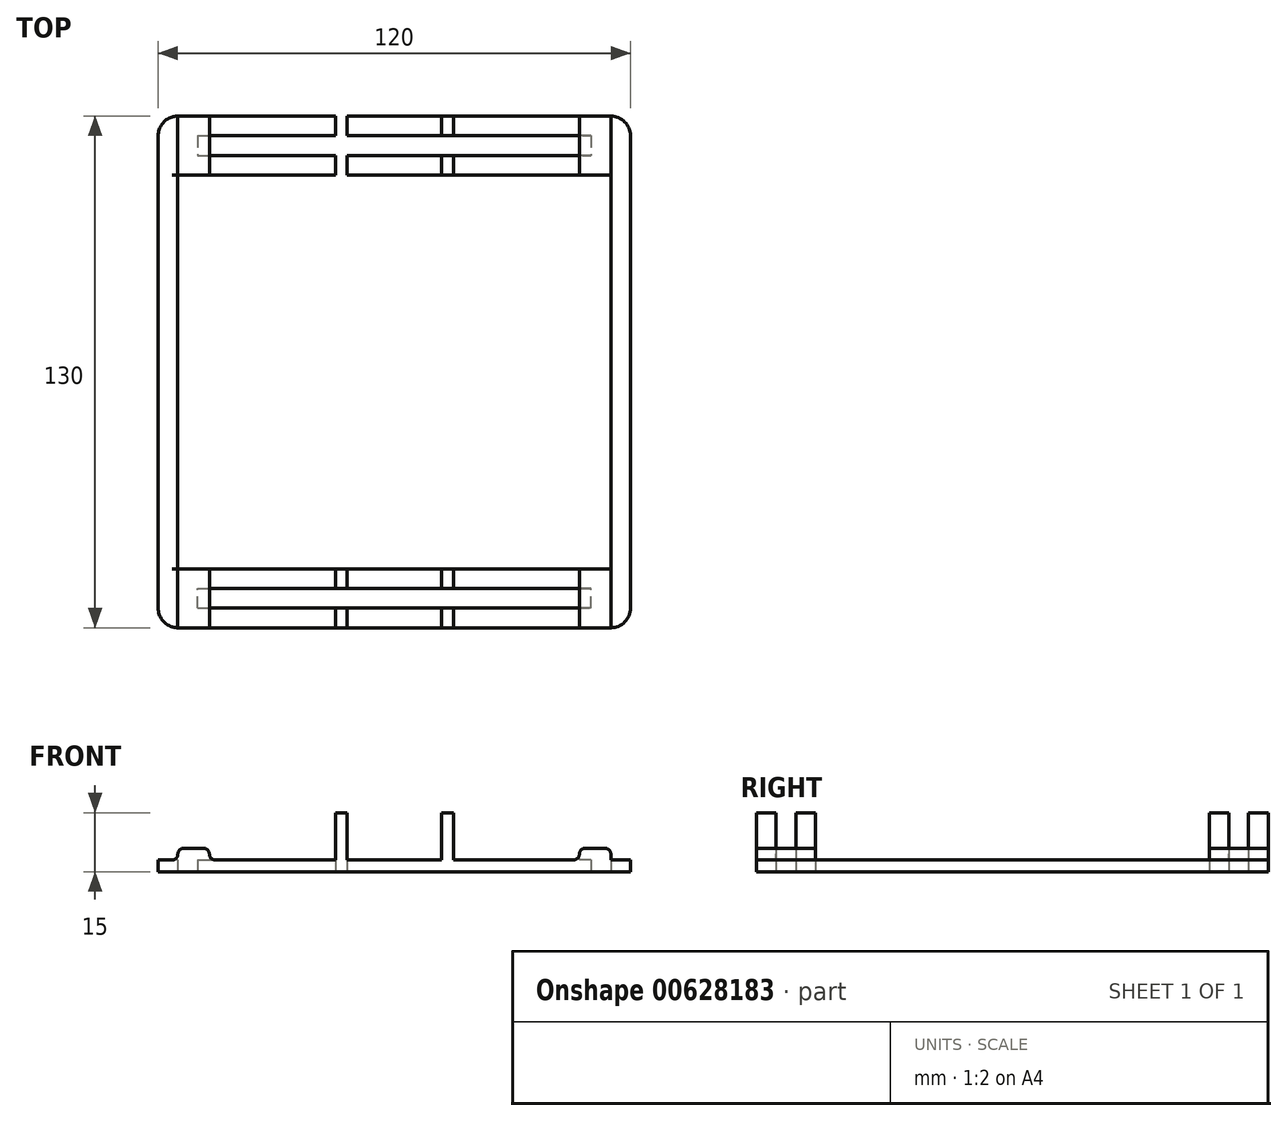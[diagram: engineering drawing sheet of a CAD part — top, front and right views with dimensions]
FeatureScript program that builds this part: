
annotation { "Feature Type Name" : "Feature", "Feature Type Description" : "" }
export const myFeature = defineFeature(function(context is Context, id is Id, definition is map)
    precondition{}
    {
        {
            var Q0;
            Q0=qCreatedBy(makeId("Top.planeOp"),FACE);
            var sketch = newSketch(context, id + "F0", { "sketchPlane" : qUnion([Q0])});
            skLineSegment(sketch, "E0.bottom", {"start": v(-50, 55) * mm, "end": v(50, 55) * mm});
            skLineSegment(sketch, "E0.left", {"start": v(-55, 50) * mm, "end": v(-55, -50) * mm});
            skLineSegment(sketch, "E0.right", {"start": v(55, 50) * mm, "end": v(55, -50) * mm});
            skPoint(sketch, "E0.middle", {"position": v(0, 0) * mm});
            skLineSegment(sketch, "E1.left", {"start": v(-60, 55) * mm, "end": v(-60, -55) * mm});
            skLineSegment(sketch, "E1.right", {"start": v(60, 55) * mm, "end": v(60, -55) * mm});
            skPoint(sketch, "E2.visualSharp", {"position": v(-55, 55) * mm});
            skPoint(sketch, "E3.visualSharp", {"position": v(-60, 60) * mm});
            skPoint(sketch, "E4.visualSharp", {"position": v(55, 55) * mm});
            skPoint(sketch, "E5.visualSharp", {"position": v(60, 60) * mm});
            skPoint(sketch, "E6.visualSharp", {"position": v(55, -55) * mm});
            skPoint(sketch, "E7.visualSharp", {"position": v(60, -60) * mm});
            skPoint(sketch, "E8.visualSharp", {"position": v(-55, -55) * mm});
            skPoint(sketch, "E9.visualSharp", {"position": v(-60, -60) * mm});
            skLineSegment(sketch, "E10", {"start": v(-55, 50) * mm, "end": v(55, 50) * mm});
            skLineSegment(sketch, "E11", {"start": v(-50, 60) * mm, "end": v(-50, 55) * mm});
            skLineSegment(sketch, "E12", {"start": v(50, 60) * mm, "end": v(50, 55) * mm});
            skPoint(sketch, "E13.bottom.end.orphan", {"position": v(15, 55) * mm});
            skPoint(sketch, "E13.bottom.start.orphan", {"position": v(-15, 55) * mm});
            skPoint(sketch, "E13.top.end.orphan", {"position": v(0, 60) * mm});
            skPoint(sketch, "E14.orphan", {"position": v(-15, 60) * mm});
            skPoint(sketch, "E15.orphan", {"position": v(15, 60) * mm});
            skPoint(sketch, "E16.MirrorCS.end.orphan", {"position": v(-15, -60) * mm});
            skPoint(sketch, "E16.MirrorCS.start.orphan", {"position": v(-15, -55) * mm});
            skPoint(sketch, "E17.MirrorCS.end.orphan", {"position": v(15, -60) * mm});
            skPoint(sketch, "E0.top.start.orphan", {"position": v(15, -55) * mm});
            skPoint(sketch, "E1.bottom.start.orphan", {"position": v(-55, 60) * mm});
            skPoint(sketch, "E18.trimOffspring.end.orphan", {"position": v(55, 60) * mm});
            skLineSegment(sketch, "E19", {"start": v(-50, 60) * mm, "end": v(50, 60) * mm});
            skPoint(sketch, "E20", {"position": v(-55, 65) * mm});
            skLineSegment(sketch, "E21", {"start": v(-55, 65) * mm, "end": v(55, 65) * mm});
            skLineSegment(sketch, "E22", {"start": v(-60, 55) * mm, "end": v(-60, 60) * mm});
            skLineSegment(sketch, "E23", {"start": v(-60, 60) * mm, "end": v(-60, 65) * mm});
            skLineSegment(sketch, "E24", {"start": v(-60, 65) * mm, "end": v(-55, 65) * mm});
            skLineSegment(sketch, "E25", {"start": v(60, 55) * mm, "end": v(60, 60) * mm});
            skLineSegment(sketch, "E26", {"start": v(60, 60) * mm, "end": v(60, 65) * mm});
            skLineSegment(sketch, "E27", {"start": v(60, 65) * mm, "end": v(55, 65) * mm});
            skLineSegment(sketch, "E28.MirrorCS", {"start": v(-55, -50) * mm, "end": v(55, -50) * mm});
            skLineSegment(sketch, "E29.MirrorCS", {"start": v(-50, -55) * mm, "end": v(50, -55) * mm});
            skLineSegment(sketch, "E30.MirrorCS", {"start": v(-50, -60) * mm, "end": v(50, -60) * mm});
            skLineSegment(sketch, "E31.MirrorCS", {"start": v(-50, -60) * mm, "end": v(-50, -55) * mm});
            skLineSegment(sketch, "E32.MirrorCS", {"start": v(50, -60) * mm, "end": v(50, -55) * mm});
            skLineSegment(sketch, "E33.MirrorCS", {"start": v(60, -55) * mm, "end": v(60, -60) * mm});
            skLineSegment(sketch, "E34.MirrorCS", {"start": v(60, -60) * mm, "end": v(60, -65) * mm});
            skLineSegment(sketch, "E35.MirrorCS", {"start": v(60, -65) * mm, "end": v(55, -65) * mm});
            skLineSegment(sketch, "E36.MirrorCS", {"start": v(-55, -65) * mm, "end": v(55, -65) * mm});
            skLineSegment(sketch, "E37.MirrorCS", {"start": v(-60, -65) * mm, "end": v(-55, -65) * mm});
            skLineSegment(sketch, "E38.MirrorCS", {"start": v(-60, -60) * mm, "end": v(-60, -65) * mm});
            skLineSegment(sketch, "E39.MirrorCS", {"start": v(-60, -55) * mm, "end": v(-60, -60) * mm});
            skLineSegment(sketch, "E40.bottom", {"start": v(-15, 55) * mm, "end": v(-12, 55) * mm});
            skLineSegment(sketch, "E40.top", {"start": v(-15, 50) * mm, "end": v(-12, 50) * mm});
            skLineSegment(sketch, "E40.left", {"start": v(-15, 55) * mm, "end": v(-15, 50) * mm});
            skLineSegment(sketch, "E40.right", {"start": v(-12, 55) * mm, "end": v(-12, 50) * mm});
            skLineSegment(sketch, "E41.MirrorCS", {"start": v(12, 55) * mm, "end": v(12, 50) * mm});
            skLineSegment(sketch, "E42.MirrorCS", {"start": v(15, 55) * mm, "end": v(15, 50) * mm});
            skLineSegment(sketch, "E43.bottom", {"start": v(-15, 60) * mm, "end": v(-12, 60) * mm});
            skLineSegment(sketch, "E43.top", {"start": v(-15, 65) * mm, "end": v(-12, 65) * mm});
            skLineSegment(sketch, "E43.left", {"start": v(-15, 60) * mm, "end": v(-15, 65) * mm});
            skLineSegment(sketch, "E43.right", {"start": v(-12, 60) * mm, "end": v(-12, 65) * mm});
            skLineSegment(sketch, "E44.MirrorCS", {"start": v(12, 60) * mm, "end": v(12, 65) * mm});
            skLineSegment(sketch, "E45.MirrorCS", {"start": v(15, 60) * mm, "end": v(15, 65) * mm});
            skLineSegment(sketch, "E46.MirrorCS", {"start": v(-15, -55) * mm, "end": v(-15, -50) * mm});
            skLineSegment(sketch, "E47.MirrorCS", {"start": v(-12, -55) * mm, "end": v(-12, -50) * mm});
            skLineSegment(sketch, "E48.MirrorCS", {"start": v(-12, -60) * mm, "end": v(-12, -65) * mm});
            skLineSegment(sketch, "E49.MirrorCS", {"start": v(-15, -60) * mm, "end": v(-15, -65) * mm});
            skLineSegment(sketch, "E50.MirrorCS", {"start": v(12, -60) * mm, "end": v(12, -65) * mm});
            skLineSegment(sketch, "E51.MirrorCS", {"start": v(15, -60) * mm, "end": v(15, -65) * mm});
            skLineSegment(sketch, "E52.MirrorCS", {"start": v(15, -55) * mm, "end": v(15, -50) * mm});
            skLineSegment(sketch, "E53.MirrorCS", {"start": v(12, -55) * mm, "end": v(12, -50) * mm});
            skSolve(sketch);
        }
        {
            var Q0;
            Q0=makeQuery(id+"F0.imprint","IMPRINT",FACE,{"disambiguationData":[TD([[makeQuery(id+"F0.imprint","IMPRINT",EDGE,{"derivedFrom":sQuery(id+"F0.wireOp",EDGE,"E0.left")}),-1.0]])]});
            var Q1;
            Q1=makeQuery(id+"F0.imprint","IMPRINT",FACE,{"disambiguationData":[TD([[makeQuery(id+"F0.imprint","IMPRINT",EDGE,{"derivedFrom":sQuery(id+"F0.wireOp",EDGE,"E0.right")}),1.0]])]});
            extrude(context, id + "F1", {"entities" : qUnion([Q0, Q1]), "depth" : 3 * mm, "offsetDistance" : 25 * mm});
        }
        {
            var Q0;
            Q0=makeQuery(id+"F0.imprint","IMPRINT",FACE,{"disambiguationData":[TD([[makeQuery(id+"F0.imprint","IMPRINT",EDGE,{"derivedFrom":sQuery(id+"F0.wireOp",EDGE,"E43.bottom")}),1.0]])]});
            var Q1;
            Q1=makeQuery(id+"F0.imprint","IMPRINT",FACE,{"disambiguationData":[TD([[makeQuery(id+"F0.imprint","IMPRINT",EDGE,{"derivedFrom":sQuery(id+"F0.wireOp",EDGE,"E40.bottom")}),-1.0]])]});
            var Q2;
            {var subQ0=sQuery(id+"F0.wireOp",EDGE,"E41.MirrorCS");Q2=makeQuery(id+"F0.imprint","IMPRINT",FACE,{"disambiguationData":[TD([[makeQuery(id+"F0.imprint","IMPRINT",EDGE,{"derivedFrom":subQ0}),1.0]])]});}
            var Q3;
            {var subQ0=sQuery(id+"F0.wireOp",EDGE,"E44.MirrorCS");Q3=makeQuery(id+"F0.imprint","IMPRINT",FACE,{"disambiguationData":[TD([[makeQuery(id+"F0.imprint","IMPRINT",EDGE,{"derivedFrom":subQ0}),-1.0]])]});}
            var Q4;
            {var subQ0=sQuery(id+"F0.wireOp",EDGE,"E52.MirrorCS");Q4=makeQuery(id+"F0.imprint","IMPRINT",FACE,{"disambiguationData":[TD([[makeQuery(id+"F0.imprint","IMPRINT",EDGE,{"derivedFrom":subQ0}),1.0]])]});}
            var Q5;
            {var subQ0=sQuery(id+"F0.wireOp",EDGE,"E50.MirrorCS");Q5=makeQuery(id+"F0.imprint","IMPRINT",FACE,{"disambiguationData":[TD([[makeQuery(id+"F0.imprint","IMPRINT",EDGE,{"derivedFrom":subQ0}),1.0]])]});}
            var Q6;
            {var subQ0=sQuery(id+"F0.wireOp",EDGE,"E48.MirrorCS");Q6=makeQuery(id+"F0.imprint","IMPRINT",FACE,{"disambiguationData":[TD([[makeQuery(id+"F0.imprint","IMPRINT",EDGE,{"derivedFrom":subQ0}),-1.0]])]});}
            var Q7;
            {var subQ0=sQuery(id+"F0.wireOp",EDGE,"E46.MirrorCS");Q7=makeQuery(id+"F0.imprint","IMPRINT",FACE,{"disambiguationData":[TD([[makeQuery(id+"F0.imprint","IMPRINT",EDGE,{"derivedFrom":subQ0}),-1.0]])]});}
            extrude(context, id + "F2", {"entities" : qUnion([Q0, Q1, Q2, Q3, Q4, Q5, Q6, Q7]), "depth" : 15 * mm, "offsetDistance" : 25 * mm});
        }
        {
            var Q0;
            {var subQ0=sQuery(id+"F0.wireOp",EDGE,"E43.right");Q0=makeQuery(id+"F0.imprint","IMPRINT",FACE,{"disambiguationData":[TD([[makeQuery(id+"F0.imprint","IMPRINT",EDGE,{"derivedFrom":subQ0}),-1.0]])]});}
            var Q1;
            {var subQ0=sQuery(id+"F0.wireOp",EDGE,"E40.right");Q1=makeQuery(id+"F0.imprint","IMPRINT",FACE,{"disambiguationData":[TD([[makeQuery(id+"F0.imprint","IMPRINT",EDGE,{"derivedFrom":subQ0}),1.0]])]});}
            var Q2;
            {var subQ0=sQuery(id+"F0.wireOp",EDGE,"E47.MirrorCS");Q2=makeQuery(id+"F0.imprint","IMPRINT",FACE,{"disambiguationData":[TD([[makeQuery(id+"F0.imprint","IMPRINT",EDGE,{"derivedFrom":subQ0}),-1.0]])]});}
            var Q3;
            {var subQ0=sQuery(id+"F0.wireOp",EDGE,"E48.MirrorCS");Q3=makeQuery(id+"F0.imprint","IMPRINT",FACE,{"disambiguationData":[TD([[makeQuery(id+"F0.imprint","IMPRINT",EDGE,{"derivedFrom":subQ0}),1.0]])]});}
            extrude(context, id + "F3", {"entities" : qUnion([Q0, Q1, Q2, Q3]), "depth" : 3 * mm, "offsetDistance" : 25 * mm});
        }
        {
            var Q0;
            Q0=makeQuery(id+"F1.opExtrude","SWEPT_EDGE",EDGE,{"disambiguationData":[OSD([sQuery(id+"F0.wireOp",EDGE,"E34.MirrorCS"),sQuery(id+"F0.wireOp",EDGE,"E35.MirrorCS")])]});
            var Q1;
            Q1=makeQuery(id+"F1.opExtrude","SWEPT_EDGE",EDGE,{"disambiguationData":[OSD([sQuery(id+"F0.wireOp",EDGE,"E26"),sQuery(id+"F0.wireOp",EDGE,"E27")])]});
            var Q2;
            Q2=makeQuery(id+"F1.opExtrude","SWEPT_EDGE",EDGE,{"disambiguationData":[OSD([sQuery(id+"F0.wireOp",EDGE,"E37.MirrorCS"),sQuery(id+"F0.wireOp",EDGE,"E38.MirrorCS")])]});
            var Q3;
            Q3=makeQuery(id+"F1.opExtrude","SWEPT_EDGE",EDGE,{"disambiguationData":[OSD([sQuery(id+"F0.wireOp",EDGE,"E23"),sQuery(id+"F0.wireOp",EDGE,"E24")])]});
            fillet(context, id + "F4", {"entities" : qUnion([Q0, Q1, Q2, Q3]), "radius" : 5 * mm, "tangentPropagation" : true, "allowEdgeOverflow" : false});
        }
        {
            var Q0;
            Q0=qCreatedBy(makeId("Front.planeOp"),FACE);
            var sketch = newSketch(context, id + "F5", { "sketchPlane" : qUnion([Q0])});
            skLineSegment(sketch, "E54.bottom", {"start": v(-55, 3) * mm, "end": v(-47, 3) * mm});
            skLineSegment(sketch, "E54.top", {"start": v(-55, 6) * mm, "end": v(-47, 6) * mm});
            skLineSegment(sketch, "E54.left", {"start": v(-55, 3) * mm, "end": v(-55, 6) * mm});
            skLineSegment(sketch, "E54.right", {"start": v(-47, 3) * mm, "end": v(-47, 6) * mm});
            skLineSegment(sketch, "E55.MirrorCS", {"start": v(55, 3) * mm, "end": v(47, 3) * mm});
            skLineSegment(sketch, "E56.MirrorCS", {"start": v(47, 3) * mm, "end": v(47, 6) * mm});
            skLineSegment(sketch, "E57.MirrorCS", {"start": v(55, 6) * mm, "end": v(47, 6) * mm});
            skLineSegment(sketch, "E58.MirrorCS", {"start": v(55, 3) * mm, "end": v(55, 6) * mm});
            skSolve(sketch);
        }
        {
            var Q0;
            Q0=makeQuery(id+"F5.imprint","IMPRINT",FACE,{"disambiguationData":[TD([[makeQuery(id+"F5.imprint","IMPRINT",EDGE,{"derivedFrom":sQuery(id+"F5.wireOp",EDGE,"E54.bottom")}),1.0]])]});
            var Q1;
            Q1=makeQuery(id+"F5.imprint","IMPRINT",FACE,{"disambiguationData":[TD([[makeQuery(id+"F5.imprint","IMPRINT",EDGE,{"derivedFrom":sQuery(id+"F5.wireOp",EDGE,"E55.MirrorCS")}),-1.0]])]});
            extrude(context, id + "F6", {"entities" : qUnion([Q0, Q1]), "depth" : 65 * mm, "offsetDistance" : 25 * mm, "hasSecondDirection" : true, "secondDirectionOppositeDirection" : true, "secondDirectionDepth" : 65 * mm});
        }
        {
            var Q0;
            {var subQ3=sQuery(id+"F0.wireOp",EDGE,"E0.left");Q0=makeQuery(id+"F0.imprint","IMPRINT",FACE,{"disambiguationData":[TD([[makeQuery(id+"F0.imprint","IMPRINT",EDGE,{"derivedFrom":subQ3}),1.0]])]});}
            extrude(context, id + "F7", {"entities" : qUnion([Q0]), "operationType" : NewBodyOperationType.REMOVE, "oppositeDirection" : true, "depth" : -6 * mm, "offsetDistance" : 25 * mm});
        }
        {
            var Q0;
            Q0=makeQuery(id+"F1.opExtrude","SWEPT_BODY",BODY,{"disambiguationData":[OSD([sQuery(id+"F0.wireOp",EDGE,"E0.bottom"),sQuery(id+"F0.wireOp",EDGE,"E0.left"),sQuery(id+"F0.wireOp",EDGE,"E1.left"),sQuery(id+"F0.wireOp",EDGE,"E10"),sQuery(id+"F0.wireOp",EDGE,"E11"),sQuery(id+"F0.wireOp",EDGE,"E19"),sQuery(id+"F0.wireOp",EDGE,"E21"),sQuery(id+"F0.wireOp",EDGE,"E22"),sQuery(id+"F0.wireOp",EDGE,"E23"),sQuery(id+"F0.wireOp",EDGE,"E24"),sQuery(id+"F0.wireOp",EDGE,"E28.MirrorCS"),sQuery(id+"F0.wireOp",EDGE,"E29.MirrorCS"),sQuery(id+"F0.wireOp",EDGE,"E30.MirrorCS"),sQuery(id+"F0.wireOp",EDGE,"E31.MirrorCS"),sQuery(id+"F0.wireOp",EDGE,"E36.MirrorCS"),sQuery(id+"F0.wireOp",EDGE,"E37.MirrorCS"),sQuery(id+"F0.wireOp",EDGE,"E38.MirrorCS"),sQuery(id+"F0.wireOp",EDGE,"E39.MirrorCS"),sQuery(id+"F0.wireOp",EDGE,"E40.left"),sQuery(id+"F0.wireOp",EDGE,"E43.left"),sQuery(id+"F0.wireOp",EDGE,"E46.MirrorCS"),sQuery(id+"F0.wireOp",EDGE,"E49.MirrorCS")])]});
            var Q1;
            Q1=makeQuery(id+"F1.opExtrude","SWEPT_BODY",BODY,{"disambiguationData":[OSD([sQuery(id+"F0.wireOp",EDGE,"E0.bottom"),sQuery(id+"F0.wireOp",EDGE,"E0.right"),sQuery(id+"F0.wireOp",EDGE,"E1.right"),sQuery(id+"F0.wireOp",EDGE,"E10"),sQuery(id+"F0.wireOp",EDGE,"E12"),sQuery(id+"F0.wireOp",EDGE,"E19"),sQuery(id+"F0.wireOp",EDGE,"E21"),sQuery(id+"F0.wireOp",EDGE,"E25"),sQuery(id+"F0.wireOp",EDGE,"E26"),sQuery(id+"F0.wireOp",EDGE,"E27"),sQuery(id+"F0.wireOp",EDGE,"E28.MirrorCS"),sQuery(id+"F0.wireOp",EDGE,"E29.MirrorCS"),sQuery(id+"F0.wireOp",EDGE,"E30.MirrorCS"),sQuery(id+"F0.wireOp",EDGE,"E32.MirrorCS"),sQuery(id+"F0.wireOp",EDGE,"E33.MirrorCS"),sQuery(id+"F0.wireOp",EDGE,"E34.MirrorCS"),sQuery(id+"F0.wireOp",EDGE,"E35.MirrorCS"),sQuery(id+"F0.wireOp",EDGE,"E36.MirrorCS"),sQuery(id+"F0.wireOp",EDGE,"E42.MirrorCS"),sQuery(id+"F0.wireOp",EDGE,"E45.MirrorCS"),sQuery(id+"F0.wireOp",EDGE,"E51.MirrorCS"),sQuery(id+"F0.wireOp",EDGE,"E52.MirrorCS")])]});
            var Q2;
            Q2=makeQuery(id+"F2.opExtrude","SWEPT_BODY",BODY,{"disambiguationData":[OSD([sQuery(id+"F0.wireOp",EDGE,"E0.bottom"),sQuery(id+"F0.wireOp",EDGE,"E10"),sQuery(id+"F0.wireOp",EDGE,"E41.MirrorCS"),sQuery(id+"F0.wireOp",EDGE,"E42.MirrorCS")])]});
            var Q3;
            Q3=makeQuery(id+"F2.opExtrude","SWEPT_BODY",BODY,{"disambiguationData":[OSD([sQuery(id+"F0.wireOp",EDGE,"E19"),sQuery(id+"F0.wireOp",EDGE,"E21"),sQuery(id+"F0.wireOp",EDGE,"E44.MirrorCS"),sQuery(id+"F0.wireOp",EDGE,"E45.MirrorCS")])]});
            var Q4;
            Q4=makeQuery(id+"F2.opExtrude","SWEPT_BODY",BODY,{"disambiguationData":[OSD([sQuery(id+"F0.wireOp",EDGE,"E28.MirrorCS"),sQuery(id+"F0.wireOp",EDGE,"E29.MirrorCS"),sQuery(id+"F0.wireOp",EDGE,"E46.MirrorCS"),sQuery(id+"F0.wireOp",EDGE,"E47.MirrorCS")])]});
            var Q5;
            Q5=makeQuery(id+"F2.opExtrude","SWEPT_BODY",BODY,{"disambiguationData":[OSD([sQuery(id+"F0.wireOp",EDGE,"E28.MirrorCS"),sQuery(id+"F0.wireOp",EDGE,"E29.MirrorCS"),sQuery(id+"F0.wireOp",EDGE,"E52.MirrorCS"),sQuery(id+"F0.wireOp",EDGE,"E53.MirrorCS")])]});
            var Q6;
            Q6=makeQuery(id+"F2.opExtrude","SWEPT_BODY",BODY,{"disambiguationData":[OSD([sQuery(id+"F0.wireOp",EDGE,"E30.MirrorCS"),sQuery(id+"F0.wireOp",EDGE,"E36.MirrorCS"),sQuery(id+"F0.wireOp",EDGE,"E48.MirrorCS"),sQuery(id+"F0.wireOp",EDGE,"E49.MirrorCS")])]});
            var Q7;
            Q7=makeQuery(id+"F2.opExtrude","SWEPT_BODY",BODY,{"disambiguationData":[OSD([sQuery(id+"F0.wireOp",EDGE,"E30.MirrorCS"),sQuery(id+"F0.wireOp",EDGE,"E36.MirrorCS"),sQuery(id+"F0.wireOp",EDGE,"E50.MirrorCS"),sQuery(id+"F0.wireOp",EDGE,"E51.MirrorCS")])]});
            var Q8;
            Q8=makeQuery(id+"F2.opExtrude","SWEPT_BODY",BODY,{"disambiguationData":[OSD([sQuery(id+"F0.wireOp",EDGE,"E40.bottom"),sQuery(id+"F0.wireOp",EDGE,"E40.top"),sQuery(id+"F0.wireOp",EDGE,"E40.left"),sQuery(id+"F0.wireOp",EDGE,"E40.right")])]});
            var Q9;
            Q9=makeQuery(id+"F2.opExtrude","SWEPT_BODY",BODY,{"disambiguationData":[OSD([sQuery(id+"F0.wireOp",EDGE,"E43.bottom"),sQuery(id+"F0.wireOp",EDGE,"E43.top"),sQuery(id+"F0.wireOp",EDGE,"E43.left"),sQuery(id+"F0.wireOp",EDGE,"E43.right")])]});
            var Q10;
            Q10=makeQuery(id+"F3.opExtrude","SWEPT_BODY",BODY,{"disambiguationData":[OSD([sQuery(id+"F0.wireOp",EDGE,"E0.bottom"),sQuery(id+"F0.wireOp",EDGE,"E10"),sQuery(id+"F0.wireOp",EDGE,"E40.right"),sQuery(id+"F0.wireOp",EDGE,"E41.MirrorCS")])]});
            var Q11;
            Q11=makeQuery(id+"F3.opExtrude","SWEPT_BODY",BODY,{"disambiguationData":[OSD([sQuery(id+"F0.wireOp",EDGE,"E19"),sQuery(id+"F0.wireOp",EDGE,"E21"),sQuery(id+"F0.wireOp",EDGE,"E43.right"),sQuery(id+"F0.wireOp",EDGE,"E44.MirrorCS")])]});
            var Q12;
            Q12=makeQuery(id+"F3.opExtrude","SWEPT_BODY",BODY,{"disambiguationData":[OSD([sQuery(id+"F0.wireOp",EDGE,"E28.MirrorCS"),sQuery(id+"F0.wireOp",EDGE,"E29.MirrorCS"),sQuery(id+"F0.wireOp",EDGE,"E47.MirrorCS"),sQuery(id+"F0.wireOp",EDGE,"E53.MirrorCS")])]});
            var Q13;
            Q13=makeQuery(id+"F3.opExtrude","SWEPT_BODY",BODY,{"disambiguationData":[OSD([sQuery(id+"F0.wireOp",EDGE,"E30.MirrorCS"),sQuery(id+"F0.wireOp",EDGE,"E36.MirrorCS"),sQuery(id+"F0.wireOp",EDGE,"E48.MirrorCS"),sQuery(id+"F0.wireOp",EDGE,"E50.MirrorCS")])]});
            var Q14;
            Q14=makeQuery(id+"F7.boolean.opBoolean","SPLIT",BODY,{"disambiguationData":[OD(0.0)],"derivedFrom":makeQuery(id+"F6.opExtrude","SWEPT_BODY",BODY,{"disambiguationData":[OSD([sQuery(id+"F5.wireOp",EDGE,"E54.bottom"),sQuery(id+"F5.wireOp",EDGE,"E54.top"),sQuery(id+"F5.wireOp",EDGE,"E54.left"),sQuery(id+"F5.wireOp",EDGE,"E54.right")])]})});
            var Q15;
            Q15=makeQuery(id+"F7.boolean.opBoolean","SPLIT",BODY,{"disambiguationData":[OD(1.0)],"derivedFrom":makeQuery(id+"F6.opExtrude","SWEPT_BODY",BODY,{"disambiguationData":[OSD([sQuery(id+"F5.wireOp",EDGE,"E54.bottom"),sQuery(id+"F5.wireOp",EDGE,"E54.top"),sQuery(id+"F5.wireOp",EDGE,"E54.left"),sQuery(id+"F5.wireOp",EDGE,"E54.right")])]})});
            var Q16;
            Q16=makeQuery(id+"F7.boolean.opBoolean","SPLIT",BODY,{"disambiguationData":[OD(0.0)],"derivedFrom":makeQuery(id+"F6.opExtrude","SWEPT_BODY",BODY,{"disambiguationData":[OSD([sQuery(id+"F5.wireOp",EDGE,"E55.MirrorCS"),sQuery(id+"F5.wireOp",EDGE,"E56.MirrorCS"),sQuery(id+"F5.wireOp",EDGE,"E57.MirrorCS"),sQuery(id+"F5.wireOp",EDGE,"E58.MirrorCS")])]})});
            var Q17;
            Q17=makeQuery(id+"F7.boolean.opBoolean","SPLIT",BODY,{"disambiguationData":[OD(1.0)],"derivedFrom":makeQuery(id+"F6.opExtrude","SWEPT_BODY",BODY,{"disambiguationData":[OSD([sQuery(id+"F5.wireOp",EDGE,"E55.MirrorCS"),sQuery(id+"F5.wireOp",EDGE,"E56.MirrorCS"),sQuery(id+"F5.wireOp",EDGE,"E57.MirrorCS"),sQuery(id+"F5.wireOp",EDGE,"E58.MirrorCS")])]})});
            booleanBodies(context, id + "F8", {"operationType" : BooleanOperationType.UNION, "tools" : qUnion([Q0, Q1, Q2, Q3, Q4, Q5, Q6, Q7, Q8, Q9, Q10, Q11, Q12, Q13, Q14, Q15, Q16, Q17])});
        }
        {
            var Q0;
            {var subQ0=sQuery(id+"F5.wireOp",EDGE,"E55.MirrorCS");var subQ1=sQuery(id+"F5.wireOp",EDGE,"E58.MirrorCS");Q0=makeQuery(id+"F7.boolean.opBoolean","SPLIT",EDGE,{"disambiguationData":[TD([makeQuery(id+"F7.opExtrude","SWEPT_FACE",FACE,{"disambiguationData":[OSD([sQuery(id+"F0.wireOp",EDGE,"E28.MirrorCS")])]})])],"derivedFrom":makeQuery(id+"F6.opExtrude","SWEPT_EDGE",EDGE,{"disambiguationData":[OSD([subQ0,subQ1])]})});}
            var Q1;
            {var subQ0=sQuery(id+"F0.wireOp",EDGE,"E28.MirrorCS");var subQ4=sQuery(id+"F0.wireOp",EDGE,"E31.MirrorCS");var subQ5=sQuery(id+"F0.wireOp",EDGE,"E29.MirrorCS");var subQ6=sQuery(id+"F0.wireOp",EDGE,"E46.MirrorCS");var subQ11=sQuery(id+"F5.wireOp",EDGE,"E54.bottom");var subQ13=sQuery(id+"F5.wireOp",EDGE,"E54.right");var subQ14=makeQuery(id+"F6.opExtrude","SWEPT_FACE",FACE,{"disambiguationData":[OSD([subQ13])]});var subQ17=makeQuery(id+"F7.opExtrude","SWEPT_FACE",FACE,{"disambiguationData":[OSD([subQ0])]});var subQ18=sQuery(id+"F0.wireOp",EDGE,"E0.left");var subQ19=makeQuery(id+"F1.opExtrude","CAP_FACE",FACE,{"disambiguationData":[OSD([sQuery(id+"F0.wireOp",EDGE,"E0.bottom"),subQ18,sQuery(id+"F0.wireOp",EDGE,"E1.left"),sQuery(id+"F0.wireOp",EDGE,"E10"),sQuery(id+"F0.wireOp",EDGE,"E11"),sQuery(id+"F0.wireOp",EDGE,"E19"),sQuery(id+"F0.wireOp",EDGE,"E21"),sQuery(id+"F0.wireOp",EDGE,"E22"),sQuery(id+"F0.wireOp",EDGE,"E23"),sQuery(id+"F0.wireOp",EDGE,"E24"),subQ0,subQ5,sQuery(id+"F0.wireOp",EDGE,"E30.MirrorCS"),subQ4,sQuery(id+"F0.wireOp",EDGE,"E36.MirrorCS"),sQuery(id+"F0.wireOp",EDGE,"E37.MirrorCS"),sQuery(id+"F0.wireOp",EDGE,"E38.MirrorCS"),sQuery(id+"F0.wireOp",EDGE,"E39.MirrorCS"),sQuery(id+"F0.wireOp",EDGE,"E40.left"),sQuery(id+"F0.wireOp",EDGE,"E43.left"),subQ6,sQuery(id+"F0.wireOp",EDGE,"E49.MirrorCS")])],"isStart":false});Q1=makeQuery(id+"F8.opBoolean","SPLIT",EDGE,{"disambiguationData":[topologyDisambiguationEdgeConnected([subQ19,subQ14]),TD([makeQuery(id+"F3.opExtrude","SWEPT_FACE",FACE,{"disambiguationData":[OSD([subQ0])]})])],"derivedFrom":makeQuery(id+"F7.boolean.opBoolean","SPLIT",EDGE,{"disambiguationData":[TD([subQ17])],"derivedFrom":makeQuery(id+"F6.opExtrude","SWEPT_EDGE",EDGE,{"disambiguationData":[OSD([subQ11,subQ13])]})})});}
            var Q2;
            {var subQ0=sQuery(id+"F0.wireOp",EDGE,"E30.MirrorCS");var subQ2=sQuery(id+"F0.wireOp",EDGE,"E49.MirrorCS");var subQ4=sQuery(id+"F0.wireOp",EDGE,"E37.MirrorCS");var subQ5=sQuery(id+"F0.wireOp",EDGE,"E36.MirrorCS");var subQ6=sQuery(id+"F0.wireOp",EDGE,"E31.MirrorCS");var subQ7=sQuery(id+"F0.wireOp",EDGE,"E28.MirrorCS");var subQ8=makeQuery(id+"F1.opExtrude","CAP_FACE",FACE,{"disambiguationData":[OSD([sQuery(id+"F0.wireOp",EDGE,"E0.bottom"),sQuery(id+"F0.wireOp",EDGE,"E0.left"),sQuery(id+"F0.wireOp",EDGE,"E1.left"),sQuery(id+"F0.wireOp",EDGE,"E10"),sQuery(id+"F0.wireOp",EDGE,"E11"),sQuery(id+"F0.wireOp",EDGE,"E19"),sQuery(id+"F0.wireOp",EDGE,"E21"),sQuery(id+"F0.wireOp",EDGE,"E22"),sQuery(id+"F0.wireOp",EDGE,"E23"),sQuery(id+"F0.wireOp",EDGE,"E24"),subQ7,sQuery(id+"F0.wireOp",EDGE,"E29.MirrorCS"),subQ0,subQ6,subQ5,subQ4,sQuery(id+"F0.wireOp",EDGE,"E38.MirrorCS"),sQuery(id+"F0.wireOp",EDGE,"E39.MirrorCS"),sQuery(id+"F0.wireOp",EDGE,"E40.left"),sQuery(id+"F0.wireOp",EDGE,"E43.left"),sQuery(id+"F0.wireOp",EDGE,"E46.MirrorCS"),subQ2])],"isStart":false});var subQ12=sQuery(id+"F5.wireOp",EDGE,"E54.bottom");var subQ14=sQuery(id+"F5.wireOp",EDGE,"E54.right");var subQ16=makeQuery(id+"F6.opExtrude","SWEPT_FACE",FACE,{"disambiguationData":[OSD([subQ14])]});Q2=makeQuery(id+"F8.opBoolean","SPLIT",EDGE,{"disambiguationData":[topologyDisambiguationEdgeConnected([subQ8,subQ16]),TD([makeQuery(id+"F3.opExtrude","SWEPT_FACE",FACE,{"disambiguationData":[OSD([subQ0])]})])],"derivedFrom":makeQuery(id+"F7.boolean.opBoolean","SPLIT",EDGE,{"disambiguationData":[TD([makeQuery(id+"F7.opExtrude","SWEPT_FACE",FACE,{"disambiguationData":[OSD([subQ7])]})])],"derivedFrom":makeQuery(id+"F6.opExtrude","SWEPT_EDGE",EDGE,{"disambiguationData":[OSD([subQ12,subQ14])]})})});}
            var Q3;
            {var subQ0=sQuery(id+"F0.wireOp",EDGE,"E52.MirrorCS");var subQ1=sQuery(id+"F0.wireOp",EDGE,"E28.MirrorCS");var subQ4=sQuery(id+"F0.wireOp",EDGE,"E29.MirrorCS");var subQ9=sQuery(id+"F5.wireOp",EDGE,"E56.MirrorCS");var subQ10=makeQuery(id+"F6.opExtrude","SWEPT_FACE",FACE,{"disambiguationData":[OSD([subQ9])]});var subQ11=sQuery(id+"F0.wireOp",EDGE,"E32.MirrorCS");var subQ13=makeQuery(id+"F7.opExtrude","SWEPT_FACE",FACE,{"disambiguationData":[OSD([subQ1])]});var subQ14=sQuery(id+"F0.wireOp",EDGE,"E0.right");var subQ15=makeQuery(id+"F1.opExtrude","CAP_FACE",FACE,{"disambiguationData":[OSD([sQuery(id+"F0.wireOp",EDGE,"E0.bottom"),subQ14,sQuery(id+"F0.wireOp",EDGE,"E1.right"),sQuery(id+"F0.wireOp",EDGE,"E10"),sQuery(id+"F0.wireOp",EDGE,"E12"),sQuery(id+"F0.wireOp",EDGE,"E19"),sQuery(id+"F0.wireOp",EDGE,"E21"),sQuery(id+"F0.wireOp",EDGE,"E25"),sQuery(id+"F0.wireOp",EDGE,"E26"),sQuery(id+"F0.wireOp",EDGE,"E27"),subQ1,subQ4,sQuery(id+"F0.wireOp",EDGE,"E30.MirrorCS"),subQ11,sQuery(id+"F0.wireOp",EDGE,"E33.MirrorCS"),sQuery(id+"F0.wireOp",EDGE,"E34.MirrorCS"),sQuery(id+"F0.wireOp",EDGE,"E35.MirrorCS"),sQuery(id+"F0.wireOp",EDGE,"E36.MirrorCS"),sQuery(id+"F0.wireOp",EDGE,"E42.MirrorCS"),sQuery(id+"F0.wireOp",EDGE,"E45.MirrorCS"),sQuery(id+"F0.wireOp",EDGE,"E51.MirrorCS"),subQ0])],"isStart":false});var subQ16=sQuery(id+"F5.wireOp",EDGE,"E55.MirrorCS");Q3=makeQuery(id+"F8.opBoolean","SPLIT",EDGE,{"disambiguationData":[topologyDisambiguationEdgeConnected([subQ15,subQ10]),TD([makeQuery(id+"F3.opExtrude","SWEPT_FACE",FACE,{"disambiguationData":[OSD([subQ1])]})])],"derivedFrom":makeQuery(id+"F7.boolean.opBoolean","SPLIT",EDGE,{"disambiguationData":[TD([subQ13])],"derivedFrom":makeQuery(id+"F6.opExtrude","SWEPT_EDGE",EDGE,{"disambiguationData":[OSD([subQ16,subQ9])]})})});}
            var Q4;
            {var subQ0=sQuery(id+"F0.wireOp",EDGE,"E30.MirrorCS");var subQ5=sQuery(id+"F0.wireOp",EDGE,"E36.MirrorCS");var subQ6=sQuery(id+"F0.wireOp",EDGE,"E51.MirrorCS");var subQ7=sQuery(id+"F0.wireOp",EDGE,"E35.MirrorCS");var subQ8=sQuery(id+"F0.wireOp",EDGE,"E32.MirrorCS");var subQ9=sQuery(id+"F0.wireOp",EDGE,"E28.MirrorCS");var subQ10=makeQuery(id+"F1.opExtrude","CAP_FACE",FACE,{"disambiguationData":[OSD([sQuery(id+"F0.wireOp",EDGE,"E0.bottom"),sQuery(id+"F0.wireOp",EDGE,"E0.right"),sQuery(id+"F0.wireOp",EDGE,"E1.right"),sQuery(id+"F0.wireOp",EDGE,"E10"),sQuery(id+"F0.wireOp",EDGE,"E12"),sQuery(id+"F0.wireOp",EDGE,"E19"),sQuery(id+"F0.wireOp",EDGE,"E21"),sQuery(id+"F0.wireOp",EDGE,"E25"),sQuery(id+"F0.wireOp",EDGE,"E26"),sQuery(id+"F0.wireOp",EDGE,"E27"),subQ9,sQuery(id+"F0.wireOp",EDGE,"E29.MirrorCS"),subQ0,subQ8,sQuery(id+"F0.wireOp",EDGE,"E33.MirrorCS"),sQuery(id+"F0.wireOp",EDGE,"E34.MirrorCS"),subQ7,subQ5,sQuery(id+"F0.wireOp",EDGE,"E42.MirrorCS"),sQuery(id+"F0.wireOp",EDGE,"E45.MirrorCS"),subQ6,sQuery(id+"F0.wireOp",EDGE,"E52.MirrorCS")])],"isStart":false});var subQ12=sQuery(id+"F5.wireOp",EDGE,"E55.MirrorCS");var subQ14=sQuery(id+"F5.wireOp",EDGE,"E56.MirrorCS");var subQ16=makeQuery(id+"F6.opExtrude","SWEPT_FACE",FACE,{"disambiguationData":[OSD([subQ14])]});Q4=makeQuery(id+"F8.opBoolean","SPLIT",EDGE,{"disambiguationData":[topologyDisambiguationEdgeConnected([subQ10,subQ16]),TD([makeQuery(id+"F3.opExtrude","SWEPT_FACE",FACE,{"disambiguationData":[OSD([subQ0])]})])],"derivedFrom":makeQuery(id+"F7.boolean.opBoolean","SPLIT",EDGE,{"disambiguationData":[TD([makeQuery(id+"F7.opExtrude","SWEPT_FACE",FACE,{"disambiguationData":[OSD([subQ9])]})])],"derivedFrom":makeQuery(id+"F6.opExtrude","SWEPT_EDGE",EDGE,{"disambiguationData":[OSD([subQ12,subQ14])]})})});}
            var Q5;
            {var subQ0=sQuery(id+"F5.wireOp",EDGE,"E54.bottom");var subQ1=sQuery(id+"F5.wireOp",EDGE,"E54.left");Q5=makeQuery(id+"F7.boolean.opBoolean","SPLIT",EDGE,{"disambiguationData":[TD([makeQuery(id+"F7.opExtrude","SWEPT_FACE",FACE,{"disambiguationData":[OSD([sQuery(id+"F0.wireOp",EDGE,"E28.MirrorCS")])]})])],"derivedFrom":makeQuery(id+"F6.opExtrude","SWEPT_EDGE",EDGE,{"disambiguationData":[OSD([subQ0,subQ1])]})});}
            var Q6;
            {var subQ0=sQuery(id+"F5.wireOp",EDGE,"E54.bottom");var subQ1=sQuery(id+"F5.wireOp",EDGE,"E54.left");Q6=makeQuery(id+"F7.boolean.opBoolean","SPLIT",EDGE,{"disambiguationData":[TD([makeQuery(id+"F7.opExtrude","SWEPT_FACE",FACE,{"disambiguationData":[OSD([sQuery(id+"F0.wireOp",EDGE,"E10"),sQuery(id+"F0.wireOp",EDGE,"E40.top")])]})])],"derivedFrom":makeQuery(id+"F6.opExtrude","SWEPT_EDGE",EDGE,{"disambiguationData":[OSD([subQ0,subQ1])]})});}
            var Q7;
            {var subQ0=sQuery(id+"F0.wireOp",EDGE,"E0.bottom");var subQ1=sQuery(id+"F0.wireOp",EDGE,"E40.top");var subQ3=sQuery(id+"F0.wireOp",EDGE,"E10");var subQ5=sQuery(id+"F0.wireOp",EDGE,"E0.right");var subQ6=sQuery(id+"F0.wireOp",EDGE,"E42.MirrorCS");var subQ7=sQuery(id+"F0.wireOp",EDGE,"E12");var subQ8=makeQuery(id+"F1.opExtrude","CAP_FACE",FACE,{"disambiguationData":[OSD([subQ0,subQ5,sQuery(id+"F0.wireOp",EDGE,"E1.right"),subQ3,subQ7,sQuery(id+"F0.wireOp",EDGE,"E19"),sQuery(id+"F0.wireOp",EDGE,"E21"),sQuery(id+"F0.wireOp",EDGE,"E25"),sQuery(id+"F0.wireOp",EDGE,"E26"),sQuery(id+"F0.wireOp",EDGE,"E27"),sQuery(id+"F0.wireOp",EDGE,"E28.MirrorCS"),sQuery(id+"F0.wireOp",EDGE,"E29.MirrorCS"),sQuery(id+"F0.wireOp",EDGE,"E30.MirrorCS"),sQuery(id+"F0.wireOp",EDGE,"E32.MirrorCS"),sQuery(id+"F0.wireOp",EDGE,"E33.MirrorCS"),sQuery(id+"F0.wireOp",EDGE,"E34.MirrorCS"),sQuery(id+"F0.wireOp",EDGE,"E35.MirrorCS"),sQuery(id+"F0.wireOp",EDGE,"E36.MirrorCS"),subQ6,sQuery(id+"F0.wireOp",EDGE,"E45.MirrorCS"),sQuery(id+"F0.wireOp",EDGE,"E51.MirrorCS"),sQuery(id+"F0.wireOp",EDGE,"E52.MirrorCS")])],"isStart":false});var subQ9=sQuery(id+"F5.wireOp",EDGE,"E55.MirrorCS");var subQ11=sQuery(id+"F5.wireOp",EDGE,"E56.MirrorCS");var subQ12=makeQuery(id+"F6.opExtrude","SWEPT_FACE",FACE,{"disambiguationData":[OSD([subQ11])]});var subQ13=makeQuery(id+"F7.opExtrude","SWEPT_FACE",FACE,{"disambiguationData":[OSD([subQ3,subQ1])]});Q7=makeQuery(id+"F8.opBoolean","SPLIT",EDGE,{"disambiguationData":[topologyDisambiguationEdgeConnected([subQ8,subQ12]),TD([makeQuery(id+"F2.opExtrude","SWEPT_FACE",FACE,{"disambiguationData":[OSD([subQ0])]})])],"derivedFrom":makeQuery(id+"F7.boolean.opBoolean","SPLIT",EDGE,{"disambiguationData":[TD([subQ13])],"derivedFrom":makeQuery(id+"F6.opExtrude","SWEPT_EDGE",EDGE,{"disambiguationData":[OSD([subQ9,subQ11])]})})});}
            var Q8;
            {var subQ0=sQuery(id+"F0.wireOp",EDGE,"E19");var subQ1=sQuery(id+"F0.wireOp",EDGE,"E21");var subQ2=sQuery(id+"F0.wireOp",EDGE,"E27");var subQ3=sQuery(id+"F5.wireOp",EDGE,"E56.MirrorCS");var subQ4=makeQuery(id+"F6.opExtrude","SWEPT_FACE",FACE,{"disambiguationData":[OSD([subQ3])]});var subQ5=sQuery(id+"F0.wireOp",EDGE,"E12");var subQ6=sQuery(id+"F0.wireOp",EDGE,"E45.MirrorCS");var subQ7=sQuery(id+"F5.wireOp",EDGE,"E55.MirrorCS");var subQ11=sQuery(id+"F0.wireOp",EDGE,"E10");var subQ12=makeQuery(id+"F1.opExtrude","CAP_FACE",FACE,{"disambiguationData":[OSD([sQuery(id+"F0.wireOp",EDGE,"E0.bottom"),sQuery(id+"F0.wireOp",EDGE,"E0.right"),sQuery(id+"F0.wireOp",EDGE,"E1.right"),subQ11,subQ5,subQ0,subQ1,sQuery(id+"F0.wireOp",EDGE,"E25"),sQuery(id+"F0.wireOp",EDGE,"E26"),subQ2,sQuery(id+"F0.wireOp",EDGE,"E28.MirrorCS"),sQuery(id+"F0.wireOp",EDGE,"E29.MirrorCS"),sQuery(id+"F0.wireOp",EDGE,"E30.MirrorCS"),sQuery(id+"F0.wireOp",EDGE,"E32.MirrorCS"),sQuery(id+"F0.wireOp",EDGE,"E33.MirrorCS"),sQuery(id+"F0.wireOp",EDGE,"E34.MirrorCS"),sQuery(id+"F0.wireOp",EDGE,"E35.MirrorCS"),sQuery(id+"F0.wireOp",EDGE,"E36.MirrorCS"),sQuery(id+"F0.wireOp",EDGE,"E42.MirrorCS"),subQ6,sQuery(id+"F0.wireOp",EDGE,"E51.MirrorCS"),sQuery(id+"F0.wireOp",EDGE,"E52.MirrorCS")])],"isStart":false});Q8=makeQuery(id+"F8.opBoolean","SPLIT",EDGE,{"disambiguationData":[topologyDisambiguationEdgeConnected([subQ12,subQ4]),TD([makeQuery(id+"F2.opExtrude","SWEPT_FACE",FACE,{"disambiguationData":[OSD([subQ0])]})])],"derivedFrom":makeQuery(id+"F7.boolean.opBoolean","SPLIT",EDGE,{"disambiguationData":[TD([makeQuery(id+"F7.opExtrude","SWEPT_FACE",FACE,{"disambiguationData":[OSD([subQ11,sQuery(id+"F0.wireOp",EDGE,"E40.top")])]})])],"derivedFrom":makeQuery(id+"F6.opExtrude","SWEPT_EDGE",EDGE,{"disambiguationData":[OSD([subQ7,subQ3])]})})});}
            var Q9;
            {var subQ0=sQuery(id+"F0.wireOp",EDGE,"E0.bottom");var subQ1=sQuery(id+"F0.wireOp",EDGE,"E40.top");var subQ2=sQuery(id+"F5.wireOp",EDGE,"E54.right");var subQ3=makeQuery(id+"F6.opExtrude","SWEPT_FACE",FACE,{"disambiguationData":[OSD([subQ2])]});var subQ5=sQuery(id+"F0.wireOp",EDGE,"E10");var subQ6=sQuery(id+"F0.wireOp",EDGE,"E0.left");var subQ7=sQuery(id+"F0.wireOp",EDGE,"E40.left");var subQ9=sQuery(id+"F0.wireOp",EDGE,"E11");var subQ10=makeQuery(id+"F1.opExtrude","CAP_FACE",FACE,{"disambiguationData":[OSD([subQ0,subQ6,sQuery(id+"F0.wireOp",EDGE,"E1.left"),subQ5,subQ9,sQuery(id+"F0.wireOp",EDGE,"E19"),sQuery(id+"F0.wireOp",EDGE,"E21"),sQuery(id+"F0.wireOp",EDGE,"E22"),sQuery(id+"F0.wireOp",EDGE,"E23"),sQuery(id+"F0.wireOp",EDGE,"E24"),sQuery(id+"F0.wireOp",EDGE,"E28.MirrorCS"),sQuery(id+"F0.wireOp",EDGE,"E29.MirrorCS"),sQuery(id+"F0.wireOp",EDGE,"E30.MirrorCS"),sQuery(id+"F0.wireOp",EDGE,"E31.MirrorCS"),sQuery(id+"F0.wireOp",EDGE,"E36.MirrorCS"),sQuery(id+"F0.wireOp",EDGE,"E37.MirrorCS"),sQuery(id+"F0.wireOp",EDGE,"E38.MirrorCS"),sQuery(id+"F0.wireOp",EDGE,"E39.MirrorCS"),subQ7,sQuery(id+"F0.wireOp",EDGE,"E43.left"),sQuery(id+"F0.wireOp",EDGE,"E46.MirrorCS"),sQuery(id+"F0.wireOp",EDGE,"E49.MirrorCS")])],"isStart":false});var subQ11=sQuery(id+"F5.wireOp",EDGE,"E54.bottom");var subQ15=makeQuery(id+"F7.opExtrude","SWEPT_FACE",FACE,{"disambiguationData":[OSD([subQ5,subQ1])]});Q9=makeQuery(id+"F8.opBoolean","SPLIT",EDGE,{"disambiguationData":[topologyDisambiguationEdgeConnected([subQ10,subQ3]),TD([makeQuery(id+"F2.opExtrude","SWEPT_FACE",FACE,{"disambiguationData":[OSD([subQ0])]})])],"derivedFrom":makeQuery(id+"F7.boolean.opBoolean","SPLIT",EDGE,{"disambiguationData":[TD([subQ15])],"derivedFrom":makeQuery(id+"F6.opExtrude","SWEPT_EDGE",EDGE,{"disambiguationData":[OSD([subQ11,subQ2])]})})});}
            var Q10;
            {var subQ0=sQuery(id+"F0.wireOp",EDGE,"E19");var subQ1=sQuery(id+"F0.wireOp",EDGE,"E21");var subQ2=sQuery(id+"F0.wireOp",EDGE,"E24");var subQ3=sQuery(id+"F5.wireOp",EDGE,"E54.right");var subQ4=makeQuery(id+"F6.opExtrude","SWEPT_FACE",FACE,{"disambiguationData":[OSD([subQ3])]});var subQ5=sQuery(id+"F0.wireOp",EDGE,"E43.left");var subQ6=sQuery(id+"F0.wireOp",EDGE,"E11");var subQ7=sQuery(id+"F0.wireOp",EDGE,"E10");var subQ8=makeQuery(id+"F1.opExtrude","CAP_FACE",FACE,{"disambiguationData":[OSD([sQuery(id+"F0.wireOp",EDGE,"E0.bottom"),sQuery(id+"F0.wireOp",EDGE,"E0.left"),sQuery(id+"F0.wireOp",EDGE,"E1.left"),subQ7,subQ6,subQ0,subQ1,sQuery(id+"F0.wireOp",EDGE,"E22"),sQuery(id+"F0.wireOp",EDGE,"E23"),subQ2,sQuery(id+"F0.wireOp",EDGE,"E28.MirrorCS"),sQuery(id+"F0.wireOp",EDGE,"E29.MirrorCS"),sQuery(id+"F0.wireOp",EDGE,"E30.MirrorCS"),sQuery(id+"F0.wireOp",EDGE,"E31.MirrorCS"),sQuery(id+"F0.wireOp",EDGE,"E36.MirrorCS"),sQuery(id+"F0.wireOp",EDGE,"E37.MirrorCS"),sQuery(id+"F0.wireOp",EDGE,"E38.MirrorCS"),sQuery(id+"F0.wireOp",EDGE,"E39.MirrorCS"),sQuery(id+"F0.wireOp",EDGE,"E40.left"),subQ5,sQuery(id+"F0.wireOp",EDGE,"E46.MirrorCS"),sQuery(id+"F0.wireOp",EDGE,"E49.MirrorCS")])],"isStart":false});var subQ10=sQuery(id+"F5.wireOp",EDGE,"E54.bottom");Q10=makeQuery(id+"F8.opBoolean","SPLIT",EDGE,{"disambiguationData":[topologyDisambiguationEdgeConnected([subQ8,subQ4]),TD([makeQuery(id+"F2.opExtrude","SWEPT_FACE",FACE,{"disambiguationData":[OSD([subQ0])]})])],"derivedFrom":makeQuery(id+"F7.boolean.opBoolean","SPLIT",EDGE,{"disambiguationData":[TD([makeQuery(id+"F7.opExtrude","SWEPT_FACE",FACE,{"disambiguationData":[OSD([subQ7,sQuery(id+"F0.wireOp",EDGE,"E40.top")])]})])],"derivedFrom":makeQuery(id+"F6.opExtrude","SWEPT_EDGE",EDGE,{"disambiguationData":[OSD([subQ10,subQ3])]})})});}
            var Q11;
            {var subQ0=sQuery(id+"F5.wireOp",EDGE,"E55.MirrorCS");var subQ1=sQuery(id+"F5.wireOp",EDGE,"E58.MirrorCS");Q11=makeQuery(id+"F7.boolean.opBoolean","SPLIT",EDGE,{"disambiguationData":[TD([makeQuery(id+"F7.opExtrude","SWEPT_FACE",FACE,{"disambiguationData":[OSD([sQuery(id+"F0.wireOp",EDGE,"E10"),sQuery(id+"F0.wireOp",EDGE,"E40.top")])]})])],"derivedFrom":makeQuery(id+"F6.opExtrude","SWEPT_EDGE",EDGE,{"disambiguationData":[OSD([subQ0,subQ1])]})});}
            var Q12;
            {var subQ0=sQuery(id+"F5.wireOp",EDGE,"E58.MirrorCS");var subQ1=sQuery(id+"F5.wireOp",EDGE,"E57.MirrorCS");Q12=makeQuery(id+"F7.boolean.opBoolean","SPLIT",EDGE,{"disambiguationData":[TD([makeQuery(id+"F7.opExtrude","SWEPT_FACE",FACE,{"disambiguationData":[OSD([sQuery(id+"F0.wireOp",EDGE,"E28.MirrorCS")])]})])],"derivedFrom":makeQuery(id+"F6.opExtrude","SWEPT_EDGE",EDGE,{"disambiguationData":[OSD([subQ1,subQ0])]})});}
            var Q13;
            {var subQ0=sQuery(id+"F5.wireOp",EDGE,"E57.MirrorCS");var subQ1=sQuery(id+"F5.wireOp",EDGE,"E56.MirrorCS");Q13=makeQuery(id+"F7.boolean.opBoolean","SPLIT",EDGE,{"disambiguationData":[TD([makeQuery(id+"F7.opExtrude","SWEPT_FACE",FACE,{"disambiguationData":[OSD([sQuery(id+"F0.wireOp",EDGE,"E28.MirrorCS")])]})])],"derivedFrom":makeQuery(id+"F6.opExtrude","SWEPT_EDGE",EDGE,{"disambiguationData":[OSD([subQ1,subQ0])]})});}
            var Q14;
            {var subQ0=sQuery(id+"F5.wireOp",EDGE,"E58.MirrorCS");var subQ1=sQuery(id+"F5.wireOp",EDGE,"E57.MirrorCS");Q14=makeQuery(id+"F7.boolean.opBoolean","SPLIT",EDGE,{"disambiguationData":[TD([makeQuery(id+"F7.opExtrude","SWEPT_FACE",FACE,{"disambiguationData":[OSD([sQuery(id+"F0.wireOp",EDGE,"E10"),sQuery(id+"F0.wireOp",EDGE,"E40.top")])]})])],"derivedFrom":makeQuery(id+"F6.opExtrude","SWEPT_EDGE",EDGE,{"disambiguationData":[OSD([subQ1,subQ0])]})});}
            var Q15;
            {var subQ0=sQuery(id+"F5.wireOp",EDGE,"E57.MirrorCS");var subQ1=sQuery(id+"F5.wireOp",EDGE,"E56.MirrorCS");Q15=makeQuery(id+"F7.boolean.opBoolean","SPLIT",EDGE,{"disambiguationData":[TD([makeQuery(id+"F7.opExtrude","SWEPT_FACE",FACE,{"disambiguationData":[OSD([sQuery(id+"F0.wireOp",EDGE,"E10"),sQuery(id+"F0.wireOp",EDGE,"E40.top")])]})])],"derivedFrom":makeQuery(id+"F6.opExtrude","SWEPT_EDGE",EDGE,{"disambiguationData":[OSD([subQ1,subQ0])]})});}
            var Q16;
            {var subQ0=sQuery(id+"F5.wireOp",EDGE,"E54.right");var subQ1=sQuery(id+"F5.wireOp",EDGE,"E54.top");Q16=makeQuery(id+"F7.boolean.opBoolean","SPLIT",EDGE,{"disambiguationData":[TD([makeQuery(id+"F7.opExtrude","SWEPT_FACE",FACE,{"disambiguationData":[OSD([sQuery(id+"F0.wireOp",EDGE,"E10"),sQuery(id+"F0.wireOp",EDGE,"E40.top")])]})])],"derivedFrom":makeQuery(id+"F6.opExtrude","SWEPT_EDGE",EDGE,{"disambiguationData":[OSD([subQ1,subQ0])]})});}
            var Q17;
            {var subQ0=sQuery(id+"F5.wireOp",EDGE,"E54.left");var subQ1=sQuery(id+"F5.wireOp",EDGE,"E54.top");Q17=makeQuery(id+"F7.boolean.opBoolean","SPLIT",EDGE,{"disambiguationData":[TD([makeQuery(id+"F7.opExtrude","SWEPT_FACE",FACE,{"disambiguationData":[OSD([sQuery(id+"F0.wireOp",EDGE,"E10"),sQuery(id+"F0.wireOp",EDGE,"E40.top")])]})])],"derivedFrom":makeQuery(id+"F6.opExtrude","SWEPT_EDGE",EDGE,{"disambiguationData":[OSD([subQ1,subQ0])]})});}
            var Q18;
            {var subQ0=sQuery(id+"F5.wireOp",EDGE,"E54.right");var subQ1=sQuery(id+"F5.wireOp",EDGE,"E54.top");Q18=makeQuery(id+"F7.boolean.opBoolean","SPLIT",EDGE,{"disambiguationData":[TD([makeQuery(id+"F7.opExtrude","SWEPT_FACE",FACE,{"disambiguationData":[OSD([sQuery(id+"F0.wireOp",EDGE,"E28.MirrorCS")])]})])],"derivedFrom":makeQuery(id+"F6.opExtrude","SWEPT_EDGE",EDGE,{"disambiguationData":[OSD([subQ1,subQ0])]})});}
            var Q19;
            {var subQ0=sQuery(id+"F5.wireOp",EDGE,"E54.left");var subQ1=sQuery(id+"F5.wireOp",EDGE,"E54.top");Q19=makeQuery(id+"F7.boolean.opBoolean","SPLIT",EDGE,{"disambiguationData":[TD([makeQuery(id+"F7.opExtrude","SWEPT_FACE",FACE,{"disambiguationData":[OSD([sQuery(id+"F0.wireOp",EDGE,"E28.MirrorCS")])]})])],"derivedFrom":makeQuery(id+"F6.opExtrude","SWEPT_EDGE",EDGE,{"disambiguationData":[OSD([subQ1,subQ0])]})});}
            fillet(context, id + "F9", {"entities" : qUnion([Q0, Q1, Q2, Q3, Q4, Q5, Q6, Q7, Q8, Q9, Q10, Q11, Q12, Q13, Q14, Q15, Q16, Q17, Q18, Q19]), "radius" : 1.5 * mm, "tangentPropagation" : true, "allowEdgeOverflow" : false});
        }
    });
